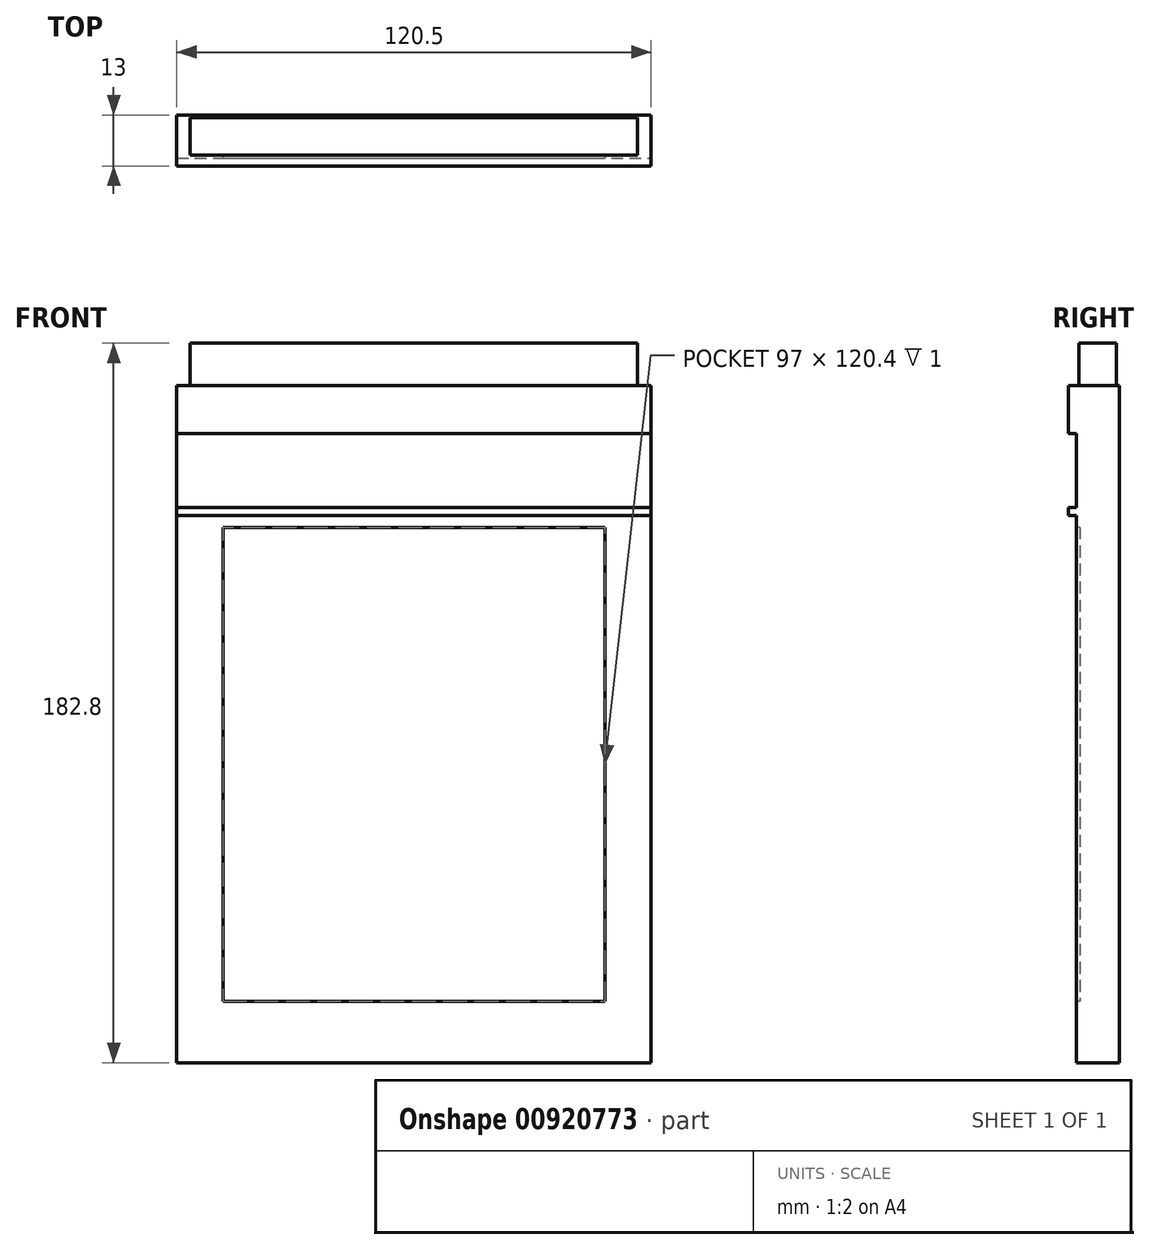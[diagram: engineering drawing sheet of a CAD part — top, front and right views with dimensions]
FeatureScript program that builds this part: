
annotation { "Feature Type Name" : "Feature", "Feature Type Description" : "" }
export const myFeature = defineFeature(function(context is Context, id is Id, definition is map)
    precondition{}
    {
        {
            var Q0;
            Q0=qCreatedBy(makeId("Front.planeOp"),FACE);
            var sketch = newSketch(context, id + "F0", { "sketchPlane" : qUnion([Q0])});
            skLineSegment(sketch, "E0.bottom", {"start": v(-126.47, 158.28) * mm, "end": v(-5.97, 158.28) * mm});
            skLineSegment(sketch, "E0.top", {"start": v(-126.47, -13.72) * mm, "end": v(-5.97, -13.72) * mm});
            skLineSegment(sketch, "E0.left", {"start": v(-126.47, 158.28) * mm, "end": v(-126.47, -13.72) * mm});
            skLineSegment(sketch, "E0.right", {"start": v(-5.97, 158.28) * mm, "end": v(-5.97, -13.72) * mm});
            skSolve(sketch);
        }
        {
            var Q0;
            Q0 = qSketchRegion(id + "F0", true);
            extrude(context, id + "F1", {"entities" : qUnion([Q0]), "depth" : 11 * mm, "offsetDistance" : 25 * mm});
        }
        {
            var Q0;
            Q0=makeQuery(id+"F1.opExtrude","CAP_FACE",FACE,{"disambiguationData":[OSD([sQuery(id+"F0.wireOp",EDGE,"E0.bottom"),sQuery(id+"F0.wireOp",EDGE,"E0.top"),sQuery(id+"F0.wireOp",EDGE,"E0.left"),sQuery(id+"F0.wireOp",EDGE,"E0.right")])],"isStart":false});
            var sketch = newSketch(context, id + "F2", { "sketchPlane" : qUnion([Q0])});
            skLineSegment(sketch, "E1.bottom", {"start": v(-114.72, 122.28) * mm, "end": v(-17.72, 122.28) * mm});
            skLineSegment(sketch, "E1.top", {"start": v(-114.72, 1.88) * mm, "end": v(-17.72, 1.88) * mm});
            skLineSegment(sketch, "E1.left", {"start": v(-114.72, 122.28) * mm, "end": v(-114.72, 1.88) * mm});
            skLineSegment(sketch, "E1.right", {"start": v(-17.72, 122.28) * mm, "end": v(-17.72, 1.88) * mm});
            skSolve(sketch);
        }
        {
            var Q0;
            Q0 = qSketchRegion(id + "F2", true);
            extrude(context, id + "F3", {"entities" : qUnion([Q0]), "operationType" : NewBodyOperationType.REMOVE, "oppositeDirection" : true, "depth" : 1 * mm, "offsetDistance" : 25 * mm});
        }
        {
            var Q0;
            Q0=makeQuery(id+"F1.opExtrude","CAP_FACE",FACE,{"disambiguationData":[OSD([sQuery(id+"F0.wireOp",EDGE,"E0.bottom"),sQuery(id+"F0.wireOp",EDGE,"E0.top"),sQuery(id+"F0.wireOp",EDGE,"E0.left"),sQuery(id+"F0.wireOp",EDGE,"E0.right")])],"isStart":false});
            var sketch = newSketch(context, id + "F4", { "sketchPlane" : qUnion([Q0])});
            skLineSegment(sketch, "E2.bottom", {"start": v(-126.47, 127.28) * mm, "end": v(-5.97, 127.28) * mm});
            skLineSegment(sketch, "E2.top", {"start": v(-126.47, 125.28) * mm, "end": v(-5.97, 125.28) * mm});
            skLineSegment(sketch, "E2.left", {"start": v(-126.47, 127.28) * mm, "end": v(-126.47, 125.28) * mm});
            skLineSegment(sketch, "E2.right", {"start": v(-5.97, 127.28) * mm, "end": v(-5.97, 125.28) * mm});
            skSolve(sketch);
        }
        {
            var Q0;
            Q0 = qSketchRegion(id + "F4", true);
            extrude(context, id + "F5", {"entities" : qUnion([Q0]), "operationType" : NewBodyOperationType.ADD, "depth" : 2 * mm, "offsetDistance" : 25 * mm});
        }
        {
            var Q0;
            Q0=makeQuery(id+"F1.opExtrude","SWEPT_FACE",FACE,{"disambiguationData":[OSD([sQuery(id+"F0.wireOp",EDGE,"E0.bottom")])]});
            var sketch = newSketch(context, id + "F6", { "sketchPlane" : qUnion([Q0])});
            skLineSegment(sketch, "E3", {"start": v(-126.47, 0) * mm, "end": v(-5.97, -11) * mm, "construction": true});
            skLineSegment(sketch, "E4.bottom", {"start": v(-9.37, -0.75) * mm, "end": v(-123.07, -0.75) * mm});
            skLineSegment(sketch, "E4.top", {"start": v(-9.37, -10.25) * mm, "end": v(-123.07, -10.25) * mm});
            skLineSegment(sketch, "E4.left", {"start": v(-9.37, -0.75) * mm, "end": v(-9.37, -10.25) * mm});
            skLineSegment(sketch, "E4.right", {"start": v(-123.07, -0.75) * mm, "end": v(-123.07, -10.25) * mm});
            skPoint(sketch, "E4.middle", {"position": v(-66.22, -5.5) * mm});
            skSolve(sketch);
        }
        {
            var Q0;
            Q0 = qSketchRegion(id + "F6", true);
            extrude(context, id + "F7", {"entities" : qUnion([Q0]), "operationType" : NewBodyOperationType.ADD, "depth" : 10.8 * mm, "offsetDistance" : 25 * mm});
        }
        {
            var Q0;
            {var subQ0=sQuery(id+"F0.wireOp",EDGE,"E0.left");var subQ1=sQuery(id+"F0.wireOp",EDGE,"E0.right");var subQ2=sQuery(id+"F0.wireOp",EDGE,"E0.bottom");Q0=makeQuery(id+"F5.boolean.opBoolean","SPLIT",FACE,{"disambiguationData":[TD([makeQuery(id+"F1.opExtrude","SWEPT_FACE",FACE,{"disambiguationData":[OSD([subQ2])]})])],"derivedFrom":makeQuery(id+"F1.opExtrude","CAP_FACE",FACE,{"disambiguationData":[OSD([subQ2,sQuery(id+"F0.wireOp",EDGE,"E0.top"),subQ0,subQ1])],"isStart":false})});}
            var sketch = newSketch(context, id + "F8", { "sketchPlane" : qUnion([Q0])});
            skLineSegment(sketch, "E5.bottom", {"start": v(-126.47, 158.28) * mm, "end": v(-5.97, 158.28) * mm});
            skLineSegment(sketch, "E5.top", {"start": v(-126.47, 146.08) * mm, "end": v(-5.97, 146.08) * mm});
            skLineSegment(sketch, "E5.left", {"start": v(-126.47, 158.28) * mm, "end": v(-126.47, 146.08) * mm});
            skLineSegment(sketch, "E5.right", {"start": v(-5.97, 158.28) * mm, "end": v(-5.97, 146.08) * mm});
            skSolve(sketch);
        }
        {
            var Q0;
            Q0 = qSketchRegion(id + "F8", true);
            extrude(context, id + "F9", {"entities" : qUnion([Q0]), "operationType" : NewBodyOperationType.ADD, "depth" : 2 * mm, "offsetDistance" : 25 * mm});
        }
    });
